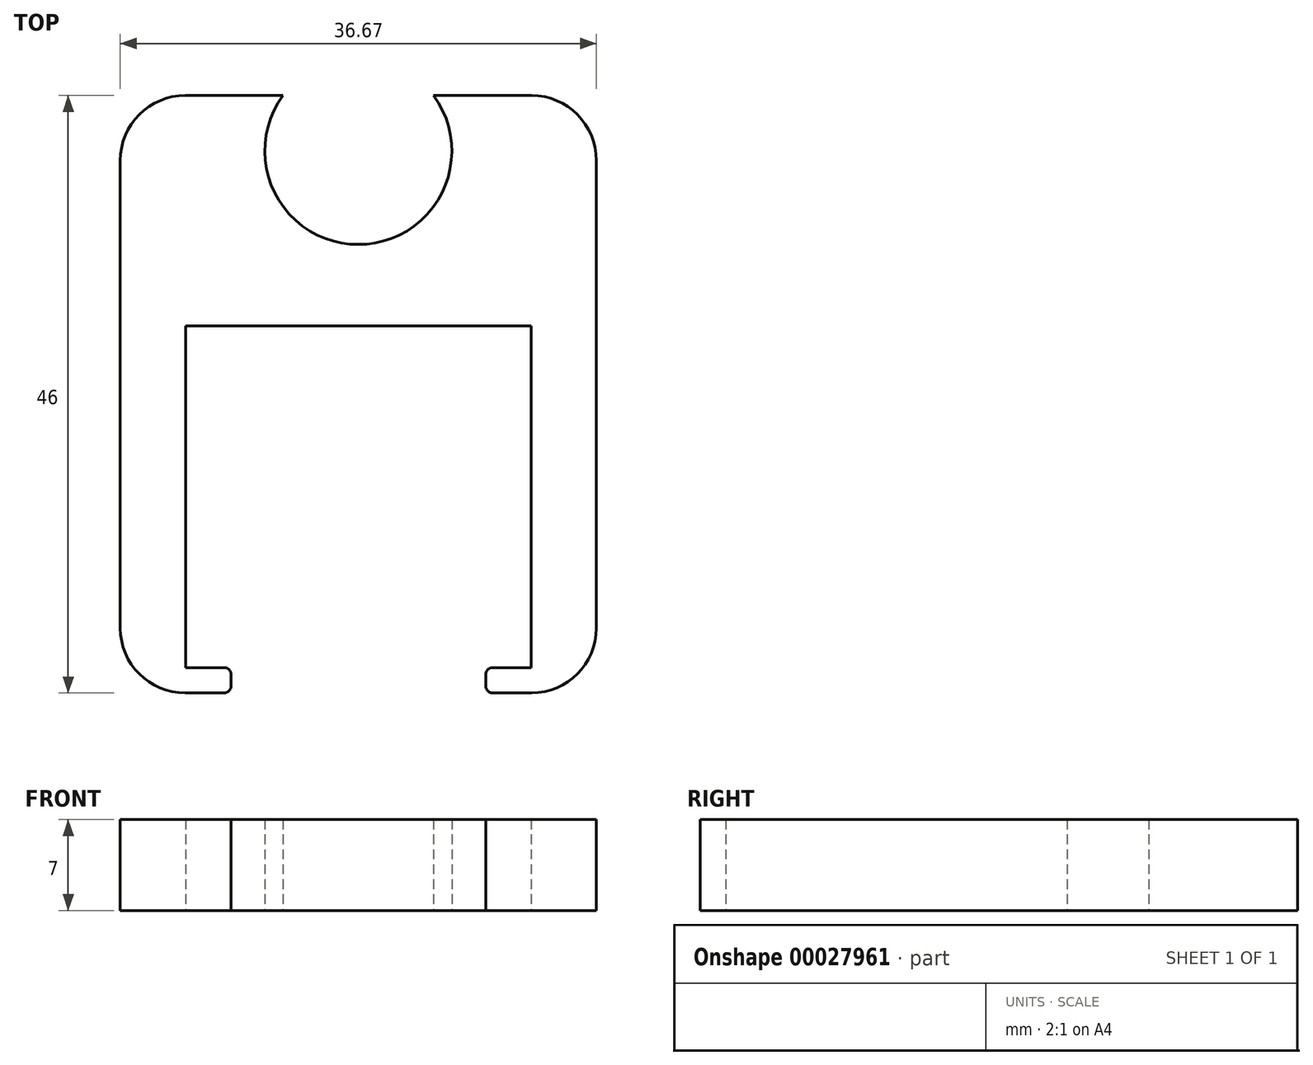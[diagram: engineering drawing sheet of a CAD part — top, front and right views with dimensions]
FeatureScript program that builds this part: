
annotation { "Feature Type Name" : "Feature", "Feature Type Description" : "" }
export const myFeature = defineFeature(function(context is Context, id is Id, definition is map)
    precondition{}
    {
        {
            var Q0;
            Q0=qCreatedBy(makeId("Top.planeOp"),FACE);
            var sketch = newSketch(context, id + "F0", { "sketchPlane" : qUnion([Q0])});
            skLineSegment(sketch, "E0.bottom", {"start": v(-5, 0) * mm, "end": v(-12.54, 0) * mm});
            skLineSegment(sketch, "E0.top", {"start": v(-5, -46) * mm, "end": v(-8, -46) * mm});
            skLineSegment(sketch, "E0.left", {"start": v(0, -5) * mm, "end": v(0, -41) * mm});
            skLineSegment(sketch, "E0.right", {"start": v(-36.67, -5) * mm, "end": v(-36.67, -41) * mm});
            skArc(sketch, "E1", {"start": v(-24.13, 0) * mm, "mid": v(-18.33, -11.47) * mm, "end": v(-12.54, 0) * mm});
            skLineSegment(sketch, "E2", {"start": v(-18.33, -17.75) * mm, "end": v(-18.33, 0) * mm, "construction": true});
            skLineSegment(sketch, "E3.trimOffspring", {"start": v(-24.13, 0) * mm, "end": v(-31.67, 0) * mm});
            skLineSegment(sketch, "E4", {"start": v(-8.52, -45.48) * mm, "end": v(-8.52, -44.57) * mm});
            skLineSegment(sketch, "E5", {"start": v(-8, -44.05) * mm, "end": v(-5.03, -44.05) * mm});
            skLineSegment(sketch, "E6", {"start": v(-5.03, -44.05) * mm, "end": v(-5.03, -17.75) * mm});
            skLineSegment(sketch, "E7", {"start": v(-5.03, -17.75) * mm, "end": v(-31.63, -17.75) * mm});
            skLineSegment(sketch, "E8", {"start": v(-31.63, -17.75) * mm, "end": v(-31.63, -44.05) * mm});
            skLineSegment(sketch, "E9", {"start": v(-31.63, -44.05) * mm, "end": v(-28.66, -44.05) * mm});
            skLineSegment(sketch, "E10", {"start": v(-28.14, -44.57) * mm, "end": v(-28.14, -45.48) * mm});
            skPoint(sketch, "E11.visualSharp", {"position": v(0, -46) * mm});
            skArc(sketch, "E11.filletArc", {"start": v(-5, -46) * mm, "mid": v(-1.46, -44.54) * mm, "end": v(0, -41) * mm});
            skPoint(sketch, "E12.visualSharp", {"position": v(0, 0) * mm});
            skArc(sketch, "E12.filletArc", {"start": v(0, -5) * mm, "mid": v(-1.46, -1.46) * mm, "end": v(-5, 0) * mm});
            skPoint(sketch, "E13.visualSharp", {"position": v(-36.67, 0) * mm});
            skArc(sketch, "E13.filletArc", {"start": v(-31.67, 0) * mm, "mid": v(-35.2, -1.46) * mm, "end": v(-36.67, -5) * mm});
            skPoint(sketch, "E14.visualSharp", {"position": v(-36.67, -46) * mm});
            skArc(sketch, "E14.filletArc", {"start": v(-36.67, -41) * mm, "mid": v(-35.2, -44.54) * mm, "end": v(-31.67, -46) * mm});
            skLineSegment(sketch, "E15.trimOffspring", {"start": v(-28.66, -46) * mm, "end": v(-31.67, -46) * mm});
            skPoint(sketch, "E16.orphan", {"position": v(-18.33, -46) * mm});
            skPoint(sketch, "E17.visualSharp", {"position": v(-8.52, -44.05) * mm});
            skPoint(sketch, "E18.visualSharp", {"position": v(-28.14, -44.05) * mm});
            skArc(sketch, "E19.filletArc", {"start": v(-8, -44.05) * mm, "mid": v(-8.37, -44.2) * mm, "end": v(-8.52, -44.57) * mm});
            skPoint(sketch, "E20.visualSharp", {"position": v(-8.52, -46) * mm});
            skArc(sketch, "E20.filletArc", {"start": v(-8.52, -45.48) * mm, "mid": v(-8.37, -45.85) * mm, "end": v(-8, -46) * mm});
            skArc(sketch, "E21.filletArc", {"start": v(-28.14, -44.57) * mm, "mid": v(-28.3, -44.2) * mm, "end": v(-28.66, -44.05) * mm});
            skPoint(sketch, "E22.visualSharp", {"position": v(-28.14, -46) * mm});
            skArc(sketch, "E22.filletArc", {"start": v(-28.66, -46) * mm, "mid": v(-28.3, -45.85) * mm, "end": v(-28.14, -45.48) * mm});
            skSolve(sketch);
        }
        {
            var Q0;
            Q0=makeQuery(id+"F0.imprint","IMPRINT",FACE,{"disambiguationData":[TD([[makeQuery(id+"F0.imprint","IMPRINT",EDGE,{"derivedFrom":sQuery(id+"F0.wireOp",EDGE,"E0.bottom")}),1.0]])]});
            extrude(context, id + "F1", {"entities" : qUnion([Q0]), "depth" : 7 * mm});
        }
    });
